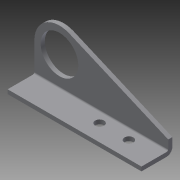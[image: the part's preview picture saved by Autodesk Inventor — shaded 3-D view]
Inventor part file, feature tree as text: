
AUTODESK INVENTOR PART (.ipt)
format: ipt  version: 2013 (Build 170138000, 138)  size: 139,264 bytes
history: native  units: in
note: dims shown in document units (in); Inventor stores cm internally (conversion verified against a paired STEP export)
features: sheet_metal_op x6, sketch x5, other x5, reference x2
ambient origin geometry x8: Origin, YZ Plane, XZ Plane, XY Plane, X Axis, Y Axis, Z Axis, Center Point
feature tree (18):
  sheet_metal_op  "Face2"
  sheet_metal_op  "Flange2"
  sheet_metal_op  "Face3"
  sketch  "Sketch1"  dims[d2=4.0in]
  other  "Plate2"
  sketch  "Sketch5"  dims[d5=0.266in]
  other  "Plate4"
  sheet_metal_op  "Bend2"
  sheet_metal_op  "Corner2"
  sketch  "Sketch6"  dims[d7=0.266in]
  sketch  "Sketch8"  dims[d9=1.5in]
  other  "Plate5"
  sheet_metal_op  "Bend3"
  sketch  "Sketch9"  dims[d18=0.125in d19=0.125in d40=0.125in d41=0.0625in d42=0.25in d43=0.125in d44=1.75in d45=90.0deg d46=0.05in d47=0.5in d48=0.125in d49=0.125in d50=1.125in d51=0.75in d52=0.75in d53=0.25in d54=0.125in d55=0.0in d57=0.75in d58=0.25in d59=0.25in d60=1.0in d61=0.125in d62=0.125in d63=0.0625in d64=0.25in d65=0.125in d66=0.125in d67=0.0in]
  reference  "Reference2"
  reference  "Reference3"
  other  "Cut3"
  other  "Cut4"
